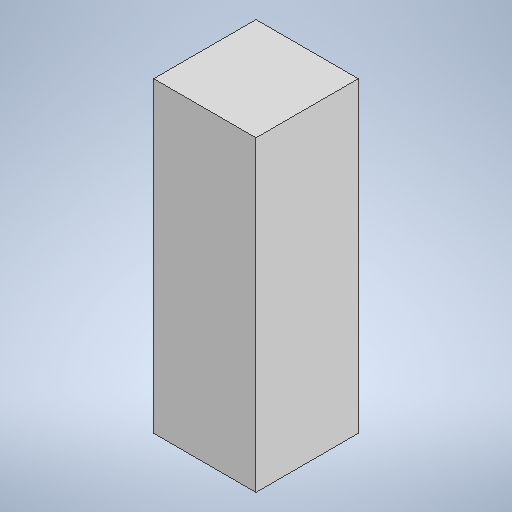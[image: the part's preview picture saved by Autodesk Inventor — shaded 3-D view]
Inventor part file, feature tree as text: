
AUTODESK INVENTOR PART (.ipt)
format: ipt  version: 2025 (Build 290162010, 162A)  size: 254,976 bytes
history: native  units: mm
features: extrude x1, sketch x1
ambient origin geometry x8: Origin, YZ Plane, XZ Plane, XY Plane, X Axis, Y Axis, Z Axis, Center Point
bodies: Solid1 (feature_tree)
feature tree (2):
  extrude  "Extrusion1"  Depth=400.0mm
  sketch  "Sketch1"  dims[d0=400.0mm d1=400.0mm d2=1200.0mm d3=0.0mm]
